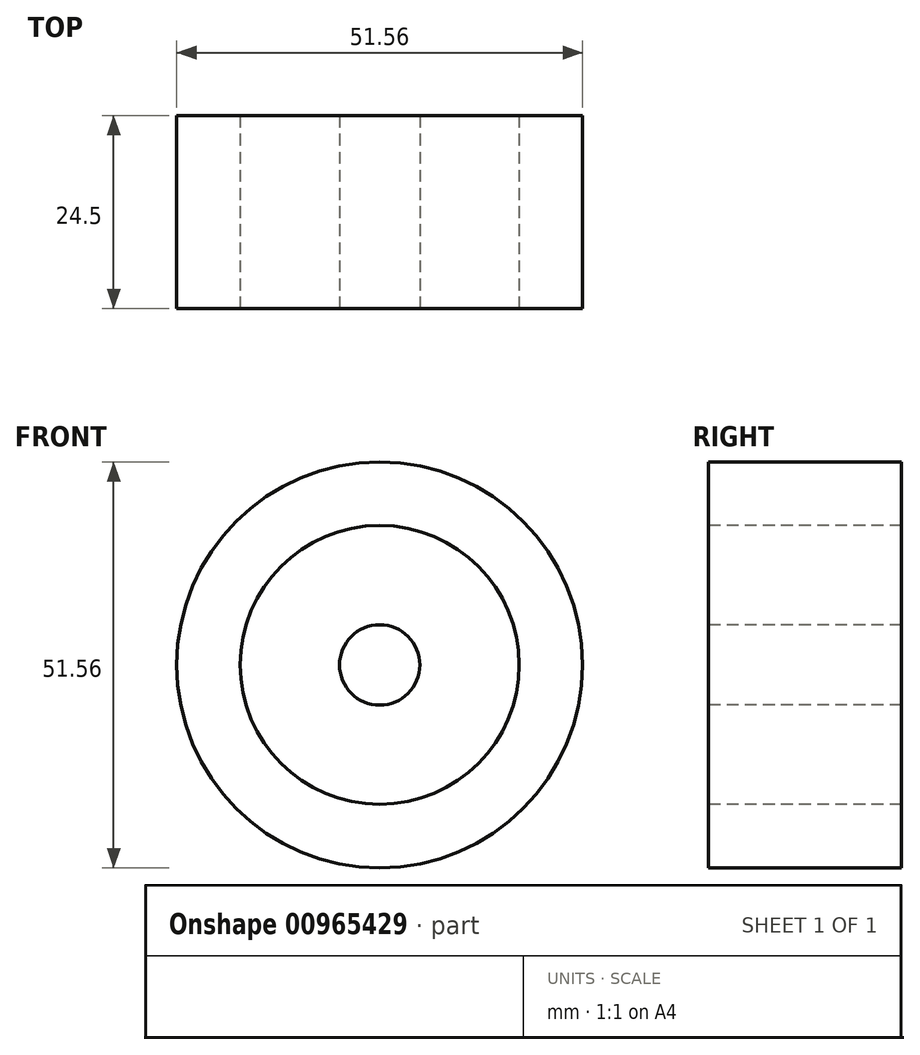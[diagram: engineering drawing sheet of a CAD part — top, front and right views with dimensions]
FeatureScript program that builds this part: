
annotation { "Feature Type Name" : "Feature", "Feature Type Description" : "" }
export const myFeature = defineFeature(function(context is Context, id is Id, definition is map)
    precondition{}
    {
        {
            var Q0;
            Q0=qCreatedBy(makeId("Front.planeOp"),FACE);
            var sketch = newSketch(context, id + "F0", { "sketchPlane" : qUnion([Q0])});
            skCircle(sketch, "E0", {"center": v(0, 0) * mm, "radius": 25.78 * mm});
            skSolve(sketch);
        }
        {
            var Q0;
            Q0=qCreatedBy(makeId("Front.planeOp"),FACE);
            var sketch = newSketch(context, id + "F1", { "sketchPlane" : qUnion([Q0])});
            skCircle(sketch, "E1", {"center": v(0, 0) * mm, "radius": 17.71 * mm});
            skCircle(sketch, "E2", {"center": v(0, 0) * mm, "radius": 5.1 * mm});
            skSolve(sketch);
        }
        {
            var Q0;
            Q0=sQuery(id+"F1.wireOp",EDGE,"E2");
            var Q1;
            Q1=sQuery(id+"F1.wireOp",EDGE,"E1");
            var Q2;
            Q2=sQuery(id+"F0.wireOp",EDGE,"E0");
            extrude(context, id + "F2", {"bodyType" : ToolBodyType.SURFACE, "surfaceEntities" : qUnion([Q0, Q1, Q2]), "depth" : 24.5 * mm, "offsetDistance" : 25.4 * mm});
        }
        {
            var Q0;
            Q0=qCreatedBy(makeId("Front.planeOp"),FACE);
            var sketch = newSketch(context, id + "F3", { "sketchPlane" : qUnion([Q0])});
            skCircle(sketch, "E3", {"center": v(47.1, 50.7) * mm, "radius": 23.1 * mm});
            skSolve(sketch);
        }
        {
            var Q0;
            Q0 = qSketchRegion(id + "F3", true);
            extrude(context, id + "F4", {"entities" : qUnion([Q0]), "depth" : 25.4 * mm, "offsetDistance" : 25.4 * mm});
        }
        {
            var Q0;
            Q0=makeQuery(id+"F4.opExtrude","CAP_FACE",FACE,{"disambiguationData":[OSD([sQuery(id+"F3.wireOp",EDGE,"E3")])],"isStart":false});
            var sketch = newSketch(context, id + "F5", { "sketchPlane" : qUnion([Q0])});
            skCircle(sketch, "E4", {"center": v(47.1, 50.7) * mm, "radius": 17.01 * mm});
            skSolve(sketch);
        }
        {
            var Q0;
            Q0 = qSketchRegion(id + "F5", true);
            extrude(context, id + "F6", {"entities" : qUnion([Q0]), "operationType" : NewBodyOperationType.ADD, "oppositeDirection" : true, "depth" : 22.42 * mm, "offsetDistance" : 25.4 * mm});
        }
        {
            var Q0;
            Q0=makeQuery(id+"F4.opExtrude","SWEPT_BODY",BODY,{"disambiguationData":[OSD([sQuery(id+"F3.wireOp",EDGE,"E3")])]});
            deleteBodies(context, id + "F7", {"entities" : qUnion([Q0])});
        }
    });
